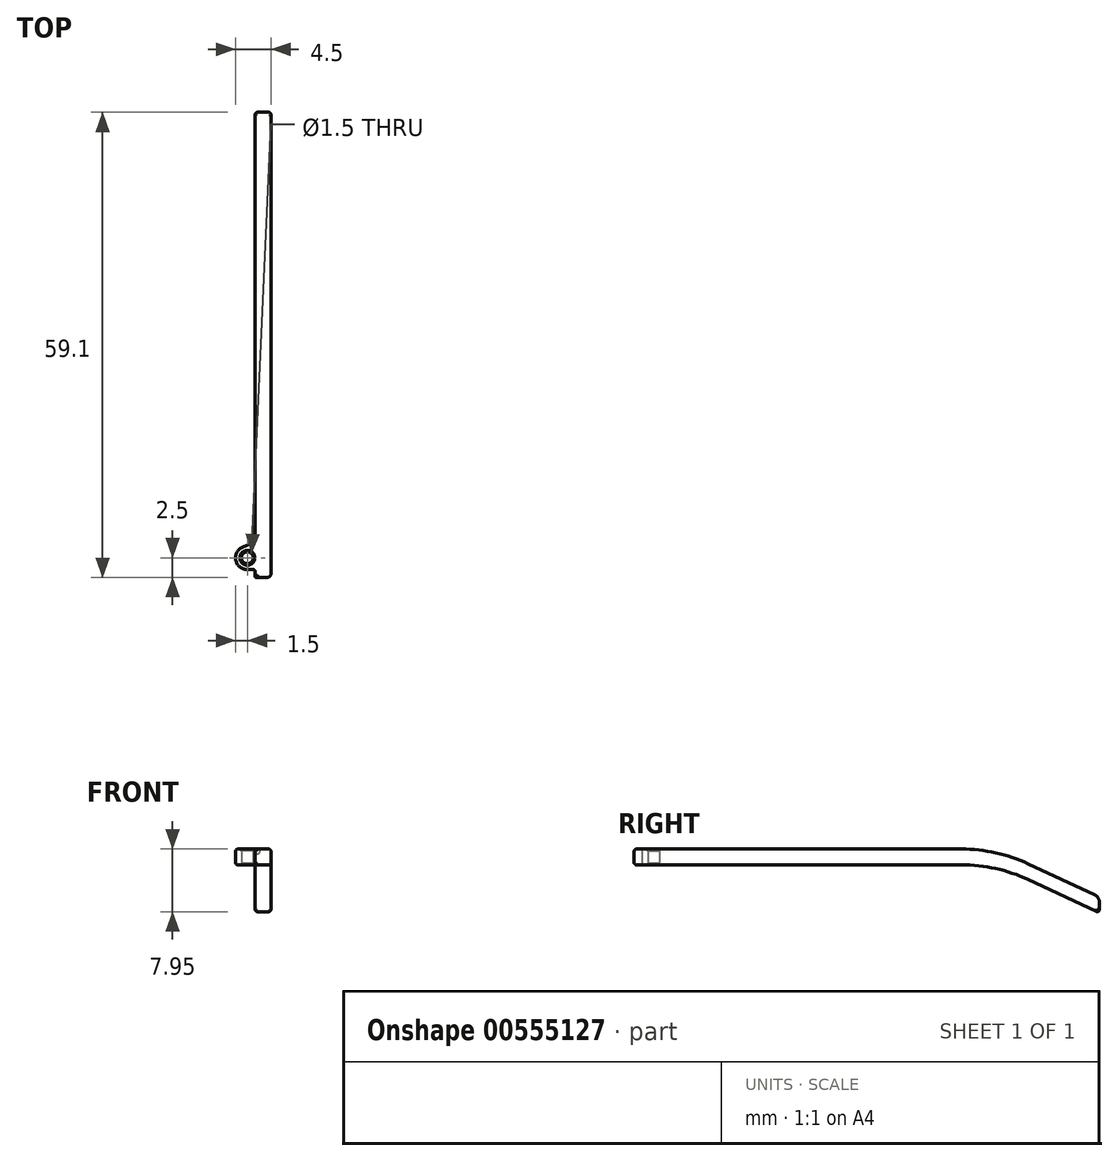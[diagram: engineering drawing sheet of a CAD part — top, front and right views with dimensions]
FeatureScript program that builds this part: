
annotation { "Feature Type Name" : "Feature", "Feature Type Description" : "" }
export const myFeature = defineFeature(function(context is Context, id is Id, definition is map)
    precondition{}
    {
        {
            var Q0;
            Q0=qCreatedBy(makeId("Top.planeOp"),FACE);
            var sketch = newSketch(context, id + "F0", { "sketchPlane" : qUnion([Q0])});
            skCircle(sketch, "E0", {"center": v(0, 0) * mm, "radius": 0.75 * mm});
            skLineSegment(sketch, "E1", {"start": v(0, -1.5) * mm, "end": v(0.75, -1.5) * mm});
            skLineSegment(sketch, "E2", {"start": v(3, -1.5) * mm, "end": v(3, 57) * mm});
            skLineSegment(sketch, "E3", {"start": v(2.5, 57.5) * mm, "end": v(1.5, 57.5) * mm});
            skLineSegment(sketch, "E4", {"start": v(1, 57) * mm, "end": v(1, 2.7) * mm});
            skLineSegment(sketch, "E5", {"start": v(0.37, 1.76) * mm, "end": v(-0.56, 1.4) * mm});
            skLineSegment(sketch, "E6", {"start": v(-1.5, 0) * mm, "end": v(-1.5, 0) * mm});
            skPoint(sketch, "E7.visualSharp", {"position": v(-1.5, -1.5) * mm});
            skArc(sketch, "E7.filletArc", {"start": v(-1.5, 0) * mm, "mid": v(-1.06, -1.06) * mm, "end": v(0, -1.5) * mm});
            skLineSegment(sketch, "E8", {"start": v(3, -1.5) * mm, "end": v(3, -2.5) * mm});
            skLineSegment(sketch, "E9", {"start": v(3, -2.5) * mm, "end": v(1.13, -2.5) * mm});
            skLineSegment(sketch, "E10", {"start": v(1, -2.37) * mm, "end": v(1, -1.75) * mm});
            skPoint(sketch, "E11.visualSharp", {"position": v(1, 2.02) * mm});
            skPoint(sketch, "E12.visualSharp", {"position": v(-1.5, 1.02) * mm});
            skPoint(sketch, "E13.visualSharp", {"position": v(1, -1.5) * mm});
            skArc(sketch, "E13.filletArc", {"start": v(1, -1.75) * mm, "mid": v(0.93, -1.57) * mm, "end": v(0.75, -1.5) * mm});
            skArc(sketch, "E14.filletArc", {"start": v(-0.56, 1.4) * mm, "mid": v(-1.24, 0.84) * mm, "end": v(-1.5, 0) * mm});
            skPoint(sketch, "E15.visualSharp", {"position": v(1, -2.5) * mm});
            skArc(sketch, "E15.filletArc", {"start": v(1, -2.37) * mm, "mid": v(1.04, -2.46) * mm, "end": v(1.13, -2.5) * mm});
            skArc(sketch, "E16.filletArc", {"start": v(0.37, 1.76) * mm, "mid": v(0.83, 2.13) * mm, "end": v(1, 2.7) * mm});
            skPoint(sketch, "E17.visualSharp", {"position": v(3, 57.5) * mm});
            skArc(sketch, "E17.filletArc", {"start": v(3, 57) * mm, "mid": v(2.85, 57.35) * mm, "end": v(2.5, 57.5) * mm});
            skPoint(sketch, "E18.visualSharp", {"position": v(1, 57.5) * mm});
            skArc(sketch, "E18.filletArc", {"start": v(1.5, 57.5) * mm, "mid": v(1.15, 57.35) * mm, "end": v(1, 57) * mm});
            skSolve(sketch);
        }
        {
            var Q0;
            Q0 = qSketchRegion(id + "F0", true);
            extrude(context, id + "F1", {"entities" : qUnion([Q0]), "depth" : 25 * mm, "offsetDistance" : 25 * mm});
        }
        {
            var Q0;
            Q0=makeQuery(id+"F1.opExtrude","SWEPT_FACE",FACE,{"disambiguationData":[OSD([sQuery(id+"F0.wireOp",EDGE,"E2"),sQuery(id+"F0.wireOp",EDGE,"E8")])]});
            var sketch = newSketch(context, id + "F2", { "sketchPlane" : qUnion([Q0])});
            skLineSegment(sketch, "E19", {"start": v(-2.5, 25) * mm, "end": v(39.1, 25) * mm});
            skLineSegment(sketch, "E20", {"start": v(47.55, 23.13) * mm, "end": v(56.02, 19.18) * mm});
            skLineSegment(sketch, "E21", {"start": v(56.6, 18.27) * mm, "end": v(56.6, 17.3) * mm});
            skLineSegment(sketch, "E22", {"start": v(56.25, 17.07) * mm, "end": v(47.55, 21.13) * mm});
            skLineSegment(sketch, "E23", {"start": v(39.1, 23) * mm, "end": v(-2.5, 23) * mm});
            skLineSegment(sketch, "E24", {"start": v(-2.5, 23) * mm, "end": v(-2.5, 25) * mm});
            skPoint(sketch, "E25.visualSharp", {"position": v(43.54, 23) * mm});
            skArc(sketch, "E25.filletArc", {"start": v(47.55, 21.13) * mm, "mid": v(43.43, 22.53) * mm, "end": v(39.1, 23) * mm});
            skPoint(sketch, "E26.visualSharp", {"position": v(43.54, 25) * mm});
            skArc(sketch, "E26.filletArc", {"start": v(47.55, 23.13) * mm, "mid": v(43.43, 24.53) * mm, "end": v(39.1, 25) * mm});
            skPoint(sketch, "E27.visualSharp", {"position": v(56.6, 16.9) * mm});
            skArc(sketch, "E27.filletArc", {"start": v(56.25, 17.07) * mm, "mid": v(56.49, 17.09) * mm, "end": v(56.6, 17.3) * mm});
            skPoint(sketch, "E28.visualSharp", {"position": v(56.6, 18.9) * mm});
            skArc(sketch, "E28.filletArc", {"start": v(56.6, 18.27) * mm, "mid": v(56.44, 18.8) * mm, "end": v(56.02, 19.18) * mm});
            skSolve(sketch);
        }
        {
            var Q0;
            Q0=makeQuery(id+"F2.imprint","IMPRINT",FACE,{"disambiguationData":[TD([[makeQuery(id+"F2.imprint","IMPRINT",EDGE,{"derivedFrom":sQuery(id+"F2.wireOp",EDGE,"E19")}),1.0]])]});
            extrude(context, id + "F3", {"entities" : qUnion([Q0]), "operationType" : NewBodyOperationType.INTERSECT, "oppositeDirection" : true, "depth" : 25 * mm, "offsetDistance" : 25 * mm});
        }
        {
            var Q0;
            Q0=makeQuery(id+"F1.opExtrude","SWEPT_EDGE",EDGE,{"disambiguationData":[OSD([sQuery(id+"F0.wireOp",EDGE,"E8"),sQuery(id+"F0.wireOp",EDGE,"E9")])]});
            fillet(context, id + "F4", {"entities" : qUnion([Q0]), "radius" : 0.5 * mm, "tangentPropagation" : true, "allowEdgeOverflow" : false});
        }
        {
            var Q0;
            Q0=makeQuery(id+"F1.opExtrude","SWEPT_FACE",FACE,{"disambiguationData":[OSD([sQuery(id+"F0.wireOp",EDGE,"E0")])]});
            chamfer(context, id + "F5", {"entities" : qUnion([Q0]), "width" : 0.2 * mm, "tangentPropagation" : true});
        }
        {
            var Q0;
            Q0=makeQuery(id+"F1.opExtrude","CAP_EDGE",EDGE,{"disambiguationData":[OSD([sQuery(id+"F0.wireOp",EDGE,"E1")])],"isStart":false});
            var Q1;
            Q1=makeQuery(id+"F3.boolean.opBoolean","COPY",EDGE,{"derivedFrom":makeQuery(id+"F3.boolean.toolComplement.opBoolean","COPY",EDGE,{"derivedFrom":makeQuery(id+"F3.opExtrude","CAP_EDGE",EDGE,{"disambiguationData":[OSD([sQuery(id+"F2.wireOp",EDGE,"E23")])],"isStart":true})})});
            fillet(context, id + "F6", {"entities" : qUnion([Q0, Q1]), "radius" : 0.3 * mm, "tangentPropagation" : true, "allowEdgeOverflow" : false});
        }
    });
